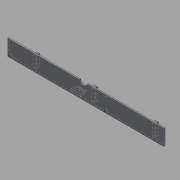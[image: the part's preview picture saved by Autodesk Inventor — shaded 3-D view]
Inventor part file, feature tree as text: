
AUTODESK INVENTOR PART (.ipt)
format: ipt  version: 2017 (Build 210142000, 142)  size: 192,512 bytes
history: native  units: mm
features: sketch x4, extrude x3, projected_geometry x2, hole x1
ambient origin geometry x8: Origin, YZ Plane, XZ Plane, XY Plane, X Axis, Y Axis, Z Axis, Center Point
bodies: Solid1 (feature_tree)
feature tree (10):
  extrude  "Extrusion1"  Depth=16.0mm
  hole  "Hole1"  [1 undecoded]
  extrude  "Extrusion2"  Depth=3.2mm
  extrude  "Extrusion3"  Depth=3.6mm
  sketch  "Sketch1"  dims[d0=158.0mm d1=16.0mm]
  sketch  "Sketch2"  dims[d2=76.5mm d3=8.2mm]
  projected_geometry  "Projected Loop1"
  sketch  "Sketch3"  dims[d4=3.2mm d5=3.2mm]
  sketch  "Sketch4"  dims[d6=1.3mm d7=0.0mm d8=154.0mm d9=1.8mm d10=1.8mm d11=57.5mm d12=1.9mm d13=6.0mm d14=4.0mm d15=2.0mm d16=90.0deg d17=8.0mm d18=20.594885mm d19=2.0mm d20=2.0mm d21=9.85mm d22=2.0mm d23=0.5mm d24=72.5mm d25=3.0mm d26=11.7mm d27=2.8mm d28=12.2mm d29=12.2mm d30=2.8mm d31=74.4mm d32=13.0mm d33=27.3mm d34=3.6mm d35=0.0mm d36=0.5mm d37=0.5mm d38=7.9mm d39=0.5mm d40=0.5mm d41=0.5mm d42=1.975mm d43=1.975mm d44=1.975mm d45=3.6mm d46=0.0mm d47=59.5mm]
  projected_geometry  "Projected Loop2"
note: 1 required parameter value undecoded (feature->parameter linkage not recoverable at this tier; creation-order binding heuristic only, values carry confidence <= 0.55)
